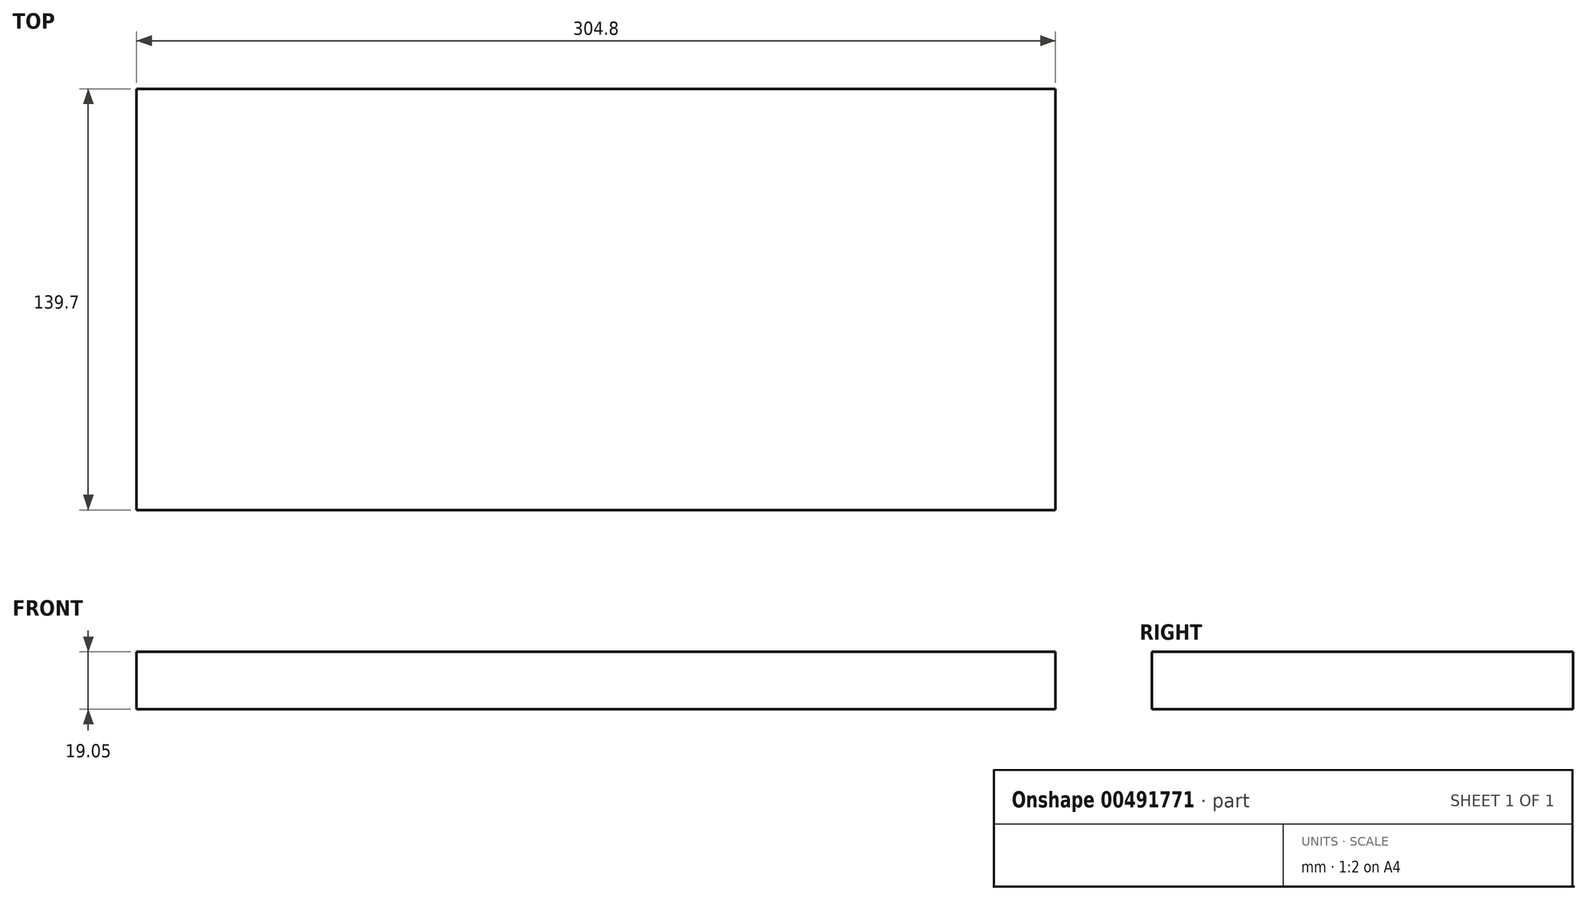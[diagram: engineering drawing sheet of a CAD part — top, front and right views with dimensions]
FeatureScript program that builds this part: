
annotation { "Feature Type Name" : "Feature", "Feature Type Description" : "" }
export const myFeature = defineFeature(function(context is Context, id is Id, definition is map)
    precondition{}
    {
        {
            var Q0;
            Q0=qCreatedBy(makeId("Top.planeOp"),FACE);
            var sketch = newSketch(context, id + "F0", { "sketchPlane" : qUnion([Q0])});
            skLineSegment(sketch, "E0.bottom", {"start": v(-108.96, 139.7) * mm, "end": v(195.84, 139.7) * mm});
            skLineSegment(sketch, "E0.top", {"start": v(-108.96, 0) * mm, "end": v(195.84, 0) * mm});
            skLineSegment(sketch, "E0.left", {"start": v(-108.96, 139.7) * mm, "end": v(-108.96, 0) * mm});
            skLineSegment(sketch, "E0.right", {"start": v(195.84, 139.7) * mm, "end": v(195.84, 0) * mm});
            skSolve(sketch);
        }
        {
            var Q0;
            Q0 = qSketchRegion(id + "F0", true);
            extrude(context, id + "F1", {"entities" : qUnion([Q0]), "depth" : 19.05 * mm});
        }
    });
